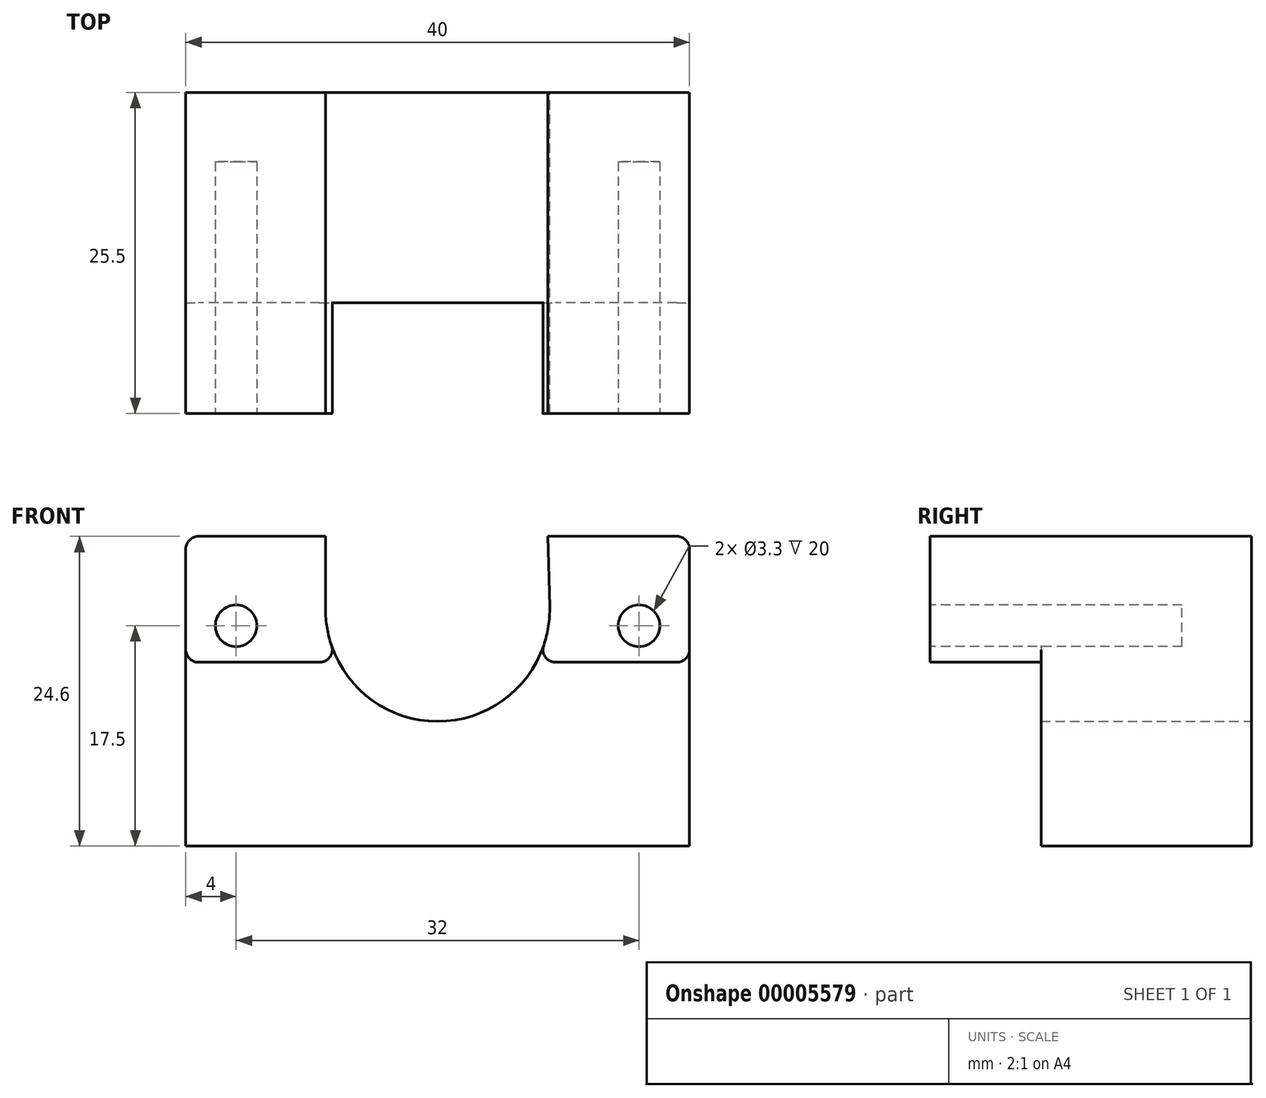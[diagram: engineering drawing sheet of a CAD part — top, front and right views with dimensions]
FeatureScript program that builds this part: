
annotation { "Feature Type Name" : "Feature", "Feature Type Description" : "" }
export const myFeature = defineFeature(function(context is Context, id is Id, definition is map)
    precondition{}
    {
        {
            var Q0;
            Q0=qCreatedBy(makeId("Right.planeOp"),FACE);
            var sketch = newSketch(context, id + "F0", { "sketchPlane" : qUnion([Q0])});
            skLineSegment(sketch, "E0", {"start": v(-8.8, 10) * mm, "end": v(16.7, 10) * mm});
            skLineSegment(sketch, "E1", {"start": v(16.7, 10) * mm, "end": v(16.7, -14.6) * mm});
            skLineSegment(sketch, "E2", {"start": v(16.7, -14.6) * mm, "end": v(0, -14.6) * mm});
            skLineSegment(sketch, "E3", {"start": v(0, -14.6) * mm, "end": v(0, 0) * mm});
            skLineSegment(sketch, "E4", {"start": v(0, 0) * mm, "end": v(-8.8, 0) * mm});
            skLineSegment(sketch, "E5", {"start": v(-8.8, 0) * mm, "end": v(-8.8, 10) * mm});
            skSolve(sketch);
        }
        {
            var Q0;
            Q0 = qSketchRegion(id + "F0", true);
            extrude(context, id + "F1", {"entities" : qUnion([Q0]), "depth" : 40 * mm});
        }
        {
            var Q0;
            Q0=makeQuery(id+"F1.opExtrude","SWEPT_FACE",FACE,{"disambiguationData":[OSD([sQuery(id+"F0.wireOp",EDGE,"E5")])]});
            var sketch = newSketch(context, id + "F2", { "sketchPlane" : qUnion([Q0])});
            skLineSegment(sketch, "E6", {"start": v(20, 0) * mm, "end": v(20, 2.9) * mm, "construction": true});
            skLineSegment(sketch, "E7", {"start": v(4, 2.9) * mm, "end": v(36, 2.9) * mm, "construction": true});
            skCircle(sketch, "E8", {"center": v(4, 2.9) * mm, "radius": 1.65 * mm});
            skCircle(sketch, "E9.0.MirrorC", {"center": v(36, 2.9) * mm, "radius": 1.65 * mm});
            skSolve(sketch);
        }
        {
            var Q0;
            Q0 = qSketchRegion(id + "F2", true);
            extrude(context, id + "F3", {"entities" : qUnion([Q0]), "operationType" : NewBodyOperationType.REMOVE, "oppositeDirection" : true, "depth" : 20 * mm});
        }
        {
            var Q0;
            Q0=makeQuery(id+"F1.opExtrude","SWEPT_FACE",FACE,{"disambiguationData":[OSD([sQuery(id+"F0.wireOp",EDGE,"E1")])]});
            var sketch = newSketch(context, id + "F4", { "sketchPlane" : qUnion([Q0])});
            skLineSegment(sketch, "E10", {"start": v(-20, 0) * mm, "end": v(-20, 4.2) * mm, "construction": true});
            skArc(sketch, "E11", {"start": v(-28.9, 4.41) * mm, "mid": v(-20.1, -4.7) * mm, "end": v(-11.1, 4.2) * mm});
            skLineSegment(sketch, "E12", {"start": v(-11.1, 4.2) * mm, "end": v(-11.1, 10) * mm});
            skLineSegment(sketch, "E13", {"start": v(-28.9, 4.41) * mm, "end": v(-28.76, 10) * mm});
            skLineSegment(sketch, "E14", {"start": v(-28.76, 10) * mm, "end": v(-11.1, 10) * mm});
            skSolve(sketch);
        }
        {
            var Q0;
            Q0=makeQuery(id+"F4.imprint","IMPRINT",FACE,{"disambiguationData":[TD([[makeQuery(id+"F4.imprint","IMPRINT",EDGE,{"derivedFrom":sQuery(id+"F4.wireOp",EDGE,"E11")}),1.0]])]});
            var Q1;
            Q1=makeQuery(id+"F1.opExtrude","SWEPT_FACE",FACE,{"disambiguationData":[OSD([sQuery(id+"F0.wireOp",EDGE,"E5")])]});
            extrude(context, id + "F5", {"entities" : qUnion([Q0]), "operationType" : NewBodyOperationType.REMOVE, "endBound" : BoundingType.UP_TO_SURFACE, "oppositeDirection" : true, "endBoundEntityFace" : qUnion([Q1]), "depth" : 25 * mm});
        }
        {
            var Q0;
            Q0=makeQuery(id+"F1.opExtrude","CAP_EDGE",EDGE,{"disambiguationData":[OSD([sQuery(id+"F0.wireOp",EDGE,"E0")])],"isStart":true});
            var Q1;
            Q1=makeQuery(id+"F1.opExtrude","CAP_EDGE",EDGE,{"disambiguationData":[OSD([sQuery(id+"F0.wireOp",EDGE,"E0")])],"isStart":false});
            var Q2;
            Q2=makeQuery(id+"F1.opExtrude","CAP_EDGE",EDGE,{"disambiguationData":[OSD([sQuery(id+"F0.wireOp",EDGE,"E4")])],"isStart":false});
            var Q3;
            Q3=makeQuery(id+"F1.opExtrude","CAP_EDGE",EDGE,{"disambiguationData":[OSD([sQuery(id+"F0.wireOp",EDGE,"E4")])],"isStart":true});
            var Q4;
            Q4=makeQuery(id+"F5.boolean.opBoolean","INTERSECT",EDGE,{"disambiguationData":[OD(0.0)],"derivedFrom":[makeQuery(id+"F1.opExtrude","SWEPT_FACE",FACE,{"disambiguationData":[OSD([sQuery(id+"F0.wireOp",EDGE,"E4")])]}),makeQuery(id+"F5.opExtrude","SWEPT_FACE",FACE,{"disambiguationData":[OSD([sQuery(id+"F4.wireOp",EDGE,"E11")])]})]});
            var Q5;
            Q5=makeQuery(id+"F5.boolean.opBoolean","INTERSECT",EDGE,{"disambiguationData":[OD(1.0)],"derivedFrom":[makeQuery(id+"F1.opExtrude","SWEPT_FACE",FACE,{"disambiguationData":[OSD([sQuery(id+"F0.wireOp",EDGE,"E4")])]}),makeQuery(id+"F5.opExtrude","SWEPT_FACE",FACE,{"disambiguationData":[OSD([sQuery(id+"F4.wireOp",EDGE,"E11")])]})]});
            var Q6;
            Q6=makeQuery(id+"F5.boolean.opBoolean","COPY",EDGE,{"derivedFrom":makeQuery(id+"F5.opExtrude","SWEPT_EDGE",EDGE,{"disambiguationData":[OSD([sQuery(id+"F0.wireOp",EDGE,"E0"),sQuery(id+"F0.wireOp",EDGE,"E1"),sQuery(id+"F4.wireOp",EDGE,"E12"),sQuery(id+"F4.wireOp",EDGE,"E14")])]})});
            var Q7;
            Q7=makeQuery(id+"F5.boolean.opBoolean","COPY",EDGE,{"derivedFrom":makeQuery(id+"F5.opExtrude","SWEPT_EDGE",EDGE,{"disambiguationData":[OSD([sQuery(id+"F0.wireOp",EDGE,"E0"),sQuery(id+"F0.wireOp",EDGE,"E1"),sQuery(id+"F4.wireOp",EDGE,"E13"),sQuery(id+"F4.wireOp",EDGE,"E14")])]})});
            fillet(context, id + "F6", {"entities" : qUnion([Q0, Q1, Q2, Q3, Q4, Q5, Q6, Q7]), "radius" : 1 * mm, "tangentPropagation" : true, "allowEdgeOverflow" : false});
        }
    });
